# Revit family: Andreu World_Raglan_BC2074
name_source: partatom
category: Mobiliario
revit_build: Autodesk Revit 2013 (Build: 20120221_2030(x64)
units: mm (PartAtom-declared; Revit-internal decimal feet)

## types (3) — shared parameters
Base Material = Andreu World Polished Aluminum
Depth = 750 mm  [stored 2.46063 ft]
Fabricante = Andreu World
Height = 430 mm
Legs Height = 240 mm  [stored 0.787402 ft]
Modelo = Raglan
Piping Material = Andreu World Leather, Black
Seat Height = 860 mm  [stored 2.82152 ft]
Seat Material = Andreu World Fabric
URL = http://www.andreuworld.com

## per-type parameters (varying)
| type | Descripción | Reference | Width |
| Andreu World_Raglan_BC2075 | 2-seater bench | BC-2075 | 1600 mm  [stored 5.24934 ft] |
| Andreu World_Raglan_BC2074 | 1-seater bench | BC-2074 | 850 mm  [stored 2.78871 ft] |
| Andreu World_Raglan_BC2076 | 3-seater bench | BC-2076 | 1950 mm  [stored 6.39764 ft] |

note: [stored X ft] marks values corroborated as IEEE doubles in the binary element streams (Revit-internal decimal feet)

## geometry (parser evidence)
native form markers: Blend x12, Sweep x2
no freeform markers — native parametric forms only
